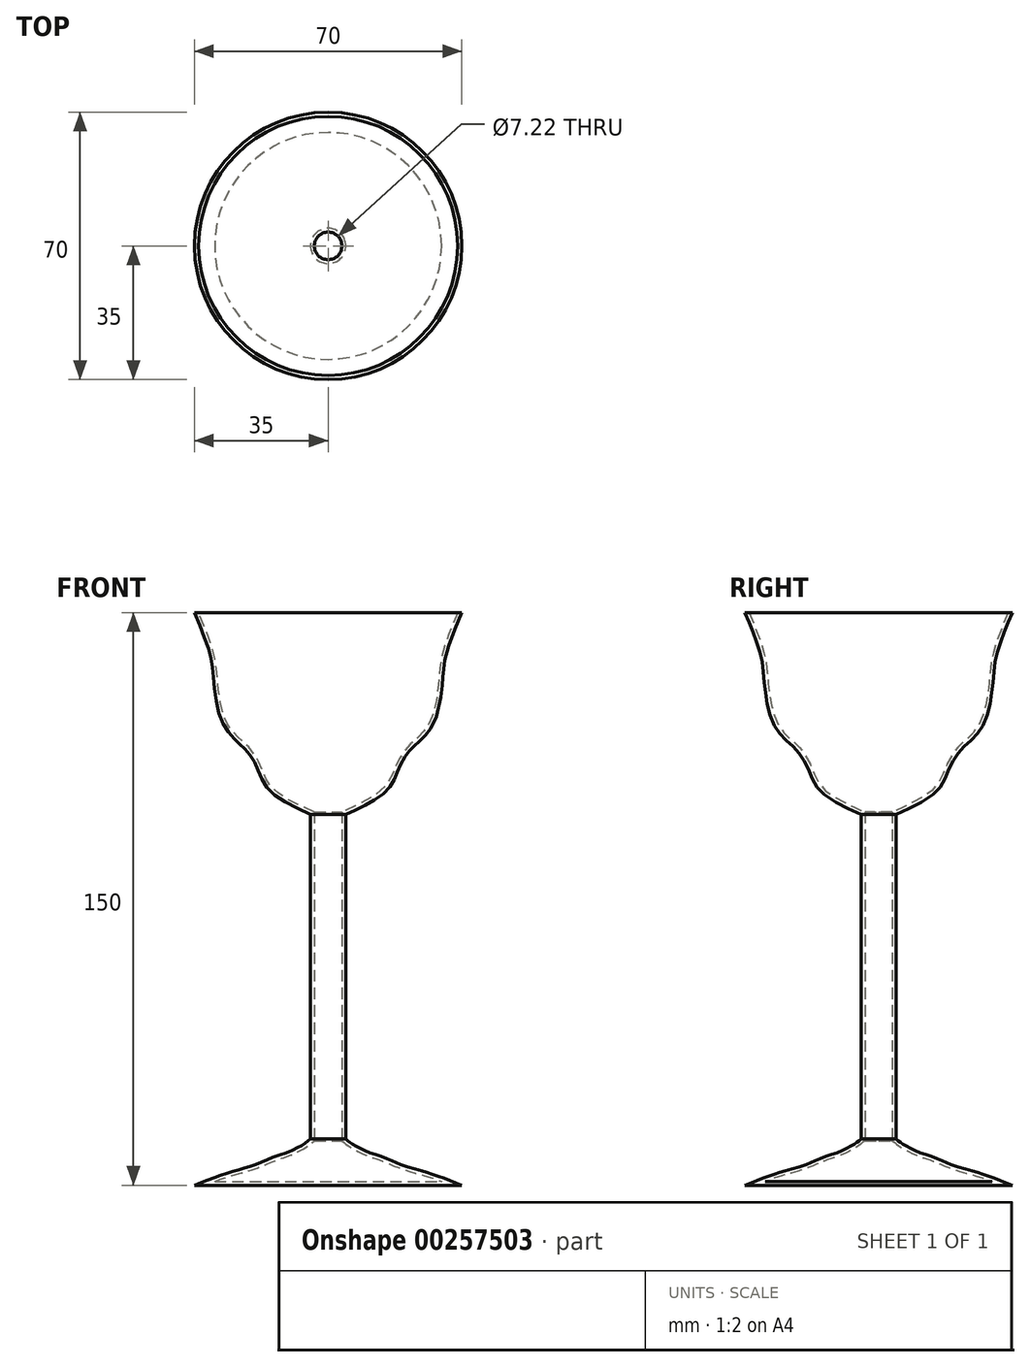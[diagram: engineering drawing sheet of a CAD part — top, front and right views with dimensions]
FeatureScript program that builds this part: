
annotation { "Feature Type Name" : "Feature", "Feature Type Description" : "" }
export const myFeature = defineFeature(function(context is Context, id is Id, definition is map)
    precondition{}
    {
        {
            var Q0;
            Q0=qCreatedBy(makeId("Front.planeOp"),FACE);
            var sketch = newSketch(context, id + "F0", { "sketchPlane" : qUnion([Q0])});
            skLineSegment(sketch, "E0.bottom", {"start": v(0, 0) * mm, "end": v(35, 0) * mm});
            skLineSegment(sketch, "E0.top", {"start": v(0, 150) * mm, "end": v(35, 150) * mm});
            skLineSegment(sketch, "E0.left", {"start": v(0, 0) * mm, "end": v(0, 150) * mm});
            skFitSpline(sketch, "E1", {"points": [v(35, 0) * mm, v(26.35, 3.23) * mm, v(19.68, 5.2) * mm, v(13.5, 7.67) * mm, v(10.54, 8.66) * mm, v(6.59, 10.64) * mm, v(4.61, 12.12) * mm], "startDerivative": vector(-40.37, 16.16) * mm, "endDerivative": vector(-14.9, 12.48) * mm});
            skLineSegment(sketch, "E2", {"start": v(4.61, 12.12) * mm, "end": v(4.61, 97.12) * mm});
            skFitSpline(sketch, "E3", {"points": [v(4.61, 97.12) * mm, v(15.49, 103.47) * mm, v(18.63, 109.36) * mm, v(21.37, 113.86) * mm, v(24.31, 116.6) * mm, v(28.04, 121.9) * mm, v(30, 132.5) * mm, v(30.98, 139.16) * mm, v(35, 150) * mm], "startDerivative": vector(80.71, 36.27) * mm, "endDerivative": vector(31.63, 76.59) * mm});
            skSolve(sketch);
        }
        {
            var Q0;
            Q0=makeQuery(id+"F0.imprint","IMPRINT",FACE,{"disambiguationData":[TD([[makeQuery(id+"F0.imprint","IMPRINT",EDGE,{"derivedFrom":sQuery(id+"F0.wireOp",EDGE,"E0.bottom")}),1.0]])]});
            var Q1;
            Q1=sQuery(id+"F0.wireOp",EDGE,"E0.left");
            revolve(context, id + "F1", {"entities" : qUnion([Q0]), "axis" : qUnion([Q1]), "revolveType" : RevolveType.FULL});
        }
        {
            var Q0;
            Q0=makeQuery(id+"F1.opRevolve","SWEPT_FACE",FACE,{"disambiguationData":[OSD([sQuery(id+"F0.wireOp",EDGE,"E0.top")])]});
            shell(context, id + "F2", {"entities" : qUnion([Q0]), "thickness" : 1 * mm});
        }
    });
